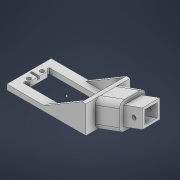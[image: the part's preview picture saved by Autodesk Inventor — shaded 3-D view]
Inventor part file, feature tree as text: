
AUTODESK INVENTOR PART (.ipt)
format: ipt  version: 2021 (Build 250183000, 183)  size: 427,008 bytes
history: native  units: mm
features: extrude x13, sketch x10, shell x1, fillet x1
ambient origin geometry x8: Origin, YZ Plane, XZ Plane, XY Plane, X Axis, Y Axis, Z Axis, Center Point
bodies: Body1 (feature_tree)
feature tree (25):
  extrude  "Extrusion2"  Depth=20.2mm
  extrude  "Extrusion3"  Depth=7.0mm
  sketch  "Skizze3"  dims[d9=4.0mm d10=0.0mm d11=3.1mm]
  extrude  "Extrusion4"  Depth=4.0mm
  extrude  "Extrusion5"  Depth=10.0mm
  sketch  "Skizze4"  dims[d12=3.1mm d15=10.0mm]
  extrude  "Extrusion6"  Depth=4.0mm TaperAngle=0.0deg
  sketch  "Skizze6"  dims[d16=5.0mm d17=4.0mm d18=0.0mm]
  extrude  "Extrusion7"  Depth=1.5mm
  extrude  "Extrusion9"  Depth=7.0mm
  shell  "Wandung2"  Thickness=2.0mm
  fillet  "Rundung1"  Radius=3.0mm
  extrude  "Extrusion10"  Depth=20.0mm
  extrude  "Extrusion11"  Depth=21.216mm
  extrude  "Extrusion12"  Depth=20.0mm TaperAngle=0.0deg
  extrude  "Extrusion14"  Depth=4.0mm
  extrude  "Extrusion15"  Depth=10.0mm
  extrude  "Extrusion13"  Depth=18.0mm
  sketch  "Skizze1"  dims[d0=41.0mm d3=20.2mm]
  sketch  "Skizze2"  dims[d7=58.0mm d8=7.0mm]
  sketch  "Skizze7"  dims[d19=7.0mm d20=1.5mm]
  sketch  "Skizze8"  dims[d21=2.0mm d22=0.0mm d23=7.0mm d24=2.0mm d25=0.0mm d26=3.0mm]
  sketch  "Skizze10"  dims[d27=21.216mm d28=20.0mm]
  sketch  "Skizze11"  dims[d29=21.216mm d30=3.490659mm]
  sketch  "Skizze12"  dims[d31=34.2mm d32=0.0mm d33=20.0mm d34=0.0mm d36=4.0mm d38=19.198622mm d42=18.0mm d44=19.198622mm d48=14.314467mm d51=13.5mm d52=0.0mm d53=2.0mm d54=2.0mm d55=0.0mm d56=2.0mm d57=0.0mm d60=3.2mm d62=27.925268mm d63=8.0mm d64=10.0mm d65=0.0mm d66=14.5mm d67=27.925268mm d68=50.0mm d69=0.0mm d70=5.0mm d71=5.0mm d81=3.0mm d82=1.2mm d83=9.434881mm d84=14.107462mm d85=10.0mm d86=0.0mm d87=40.0mm d88=0.0mm]
